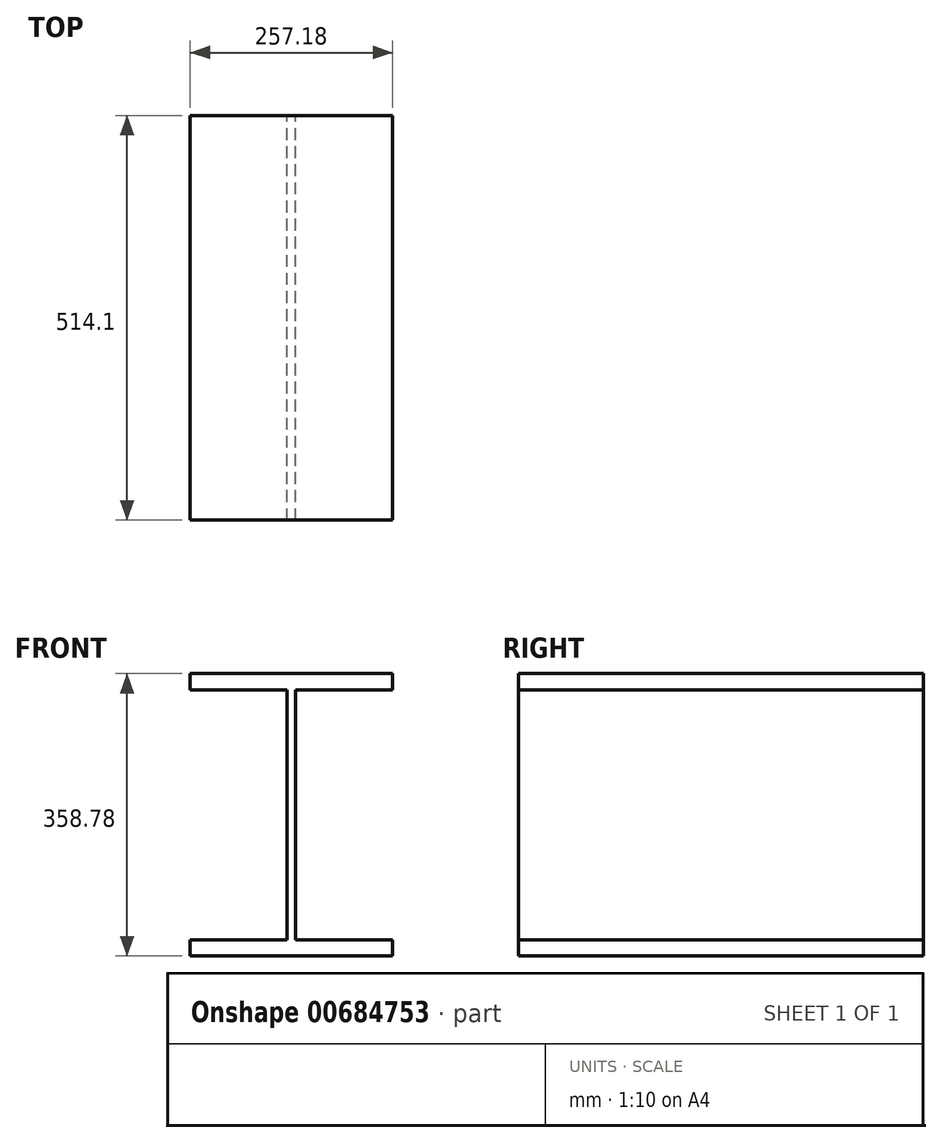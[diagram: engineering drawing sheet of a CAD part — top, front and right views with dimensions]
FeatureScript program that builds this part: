
annotation { "Feature Type Name" : "Feature", "Feature Type Description" : "" }
export const myFeature = defineFeature(function(context is Context, id is Id, definition is map)
    precondition{}
    {
        {
            var Q0;
            Q0=qCreatedBy(makeId("Front.planeOp"),FACE);
            var sketch = newSketch(context, id + "F0", { "sketchPlane" : qUnion([Q0])});
            skLineSegment(sketch, "E0", {"start": v(-128.59, 179.39) * mm, "end": v(128.59, 179.39) * mm});
            skLineSegment(sketch, "E1", {"start": v(128.59, 179.39) * mm, "end": v(128.59, 158.75) * mm});
            skLineSegment(sketch, "E2", {"start": v(128.59, 158.75) * mm, "end": v(5.56, 158.75) * mm});
            skLineSegment(sketch, "E3", {"start": v(5.56, 158.75) * mm, "end": v(5.56, -158.75) * mm});
            skLineSegment(sketch, "E4", {"start": v(5.56, -158.75) * mm, "end": v(128.59, -158.75) * mm});
            skLineSegment(sketch, "E5", {"start": v(-128.59, 179.39) * mm, "end": v(-128.59, 158.75) * mm});
            skLineSegment(sketch, "E6", {"start": v(-128.59, 158.75) * mm, "end": v(-5.56, 158.75) * mm});
            skLineSegment(sketch, "E7", {"start": v(-5.56, 158.75) * mm, "end": v(-5.56, -158.75) * mm});
            skLineSegment(sketch, "E8", {"start": v(-5.56, -158.75) * mm, "end": v(-128.59, -158.75) * mm});
            skLineSegment(sketch, "E9", {"start": v(-128.59, -158.75) * mm, "end": v(-128.59, -179.39) * mm});
            skLineSegment(sketch, "E10", {"start": v(-128.59, -179.39) * mm, "end": v(128.59, -179.39) * mm});
            skLineSegment(sketch, "E11", {"start": v(128.59, -179.39) * mm, "end": v(128.59, -158.75) * mm});
            skLineSegment(sketch, "E12", {"start": v(5.56, 158.75) * mm, "end": v(-5.56, -158.75) * mm, "construction": true});
            skSolve(sketch);
        }
        {
            var Q0;
            Q0=qSketchRegion(id+"F0",true);
            extrude(context, id + "F1", {"entities" : qUnion([Q0]), "depth" : 514.1 * mm, "offsetDistance" : 25.4 * mm});
        }
    });
